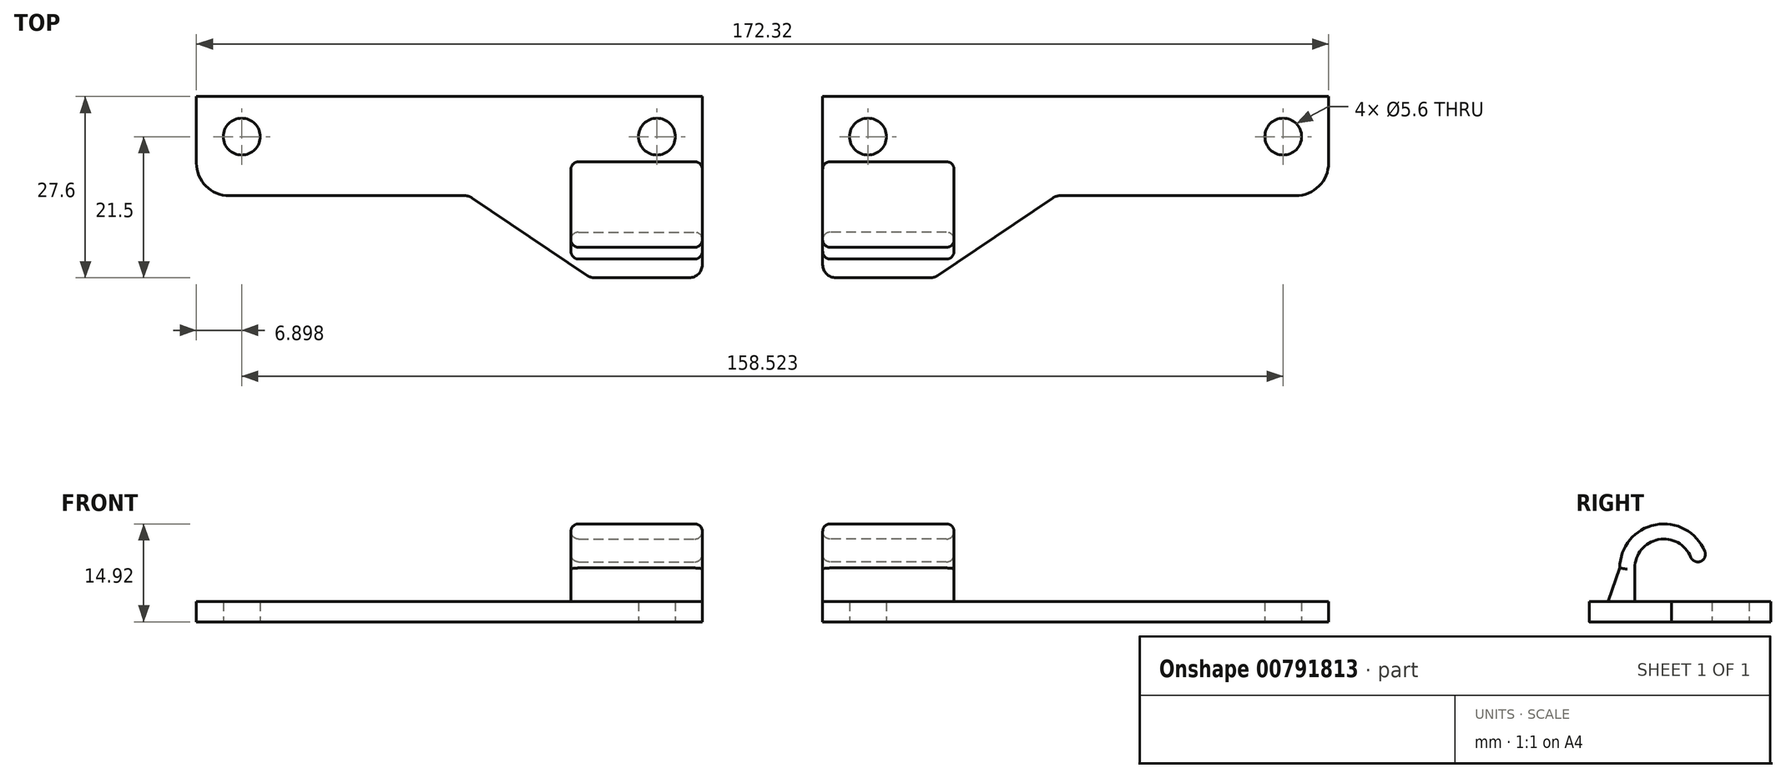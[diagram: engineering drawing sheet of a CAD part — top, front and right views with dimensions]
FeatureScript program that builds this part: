
annotation { "Feature Type Name" : "Feature", "Feature Type Description" : "" }
export const myFeature = defineFeature(function(context is Context, id is Id, definition is map)
    precondition{}
    {
        {
            var Q0;
            Q0=qCreatedBy(makeId("Top.planeOp"),FACE);
            var sketch = newSketch(context, id + "F0", { "sketchPlane" : qUnion([Q0])});
            skLineSegment(sketch, "E0.bottom", {"start": v(-29.06, 27.5) * mm, "end": v(37.94, 27.5) * mm});
            skCircle(sketch, "E1", {"center": v(-27.16, 21.4) * mm, "radius": 2.8 * mm});
            skLineSegment(sketch, "E2", {"start": v(36.74, 27.5) * mm, "end": v(36.74, 21.3) * mm});
            skCircle(sketch, "E3", {"center": v(36.04, 21.4) * mm, "radius": 2.8 * mm});
            skPoint(sketch, "E4.visualSharp", {"position": v(-34.06, 27.5) * mm});
            skPoint(sketch, "E5.visualSharp", {"position": v(42.94, 27.5) * mm});
            skLineSegment(sketch, "E6", {"start": v(-34.06, 22.5) * mm, "end": v(-34.06, 17.4) * mm});
            skLineSegment(sketch, "E7", {"start": v(42.94, 12.4) * mm, "end": v(42.94, 22.5) * mm});
            skLineSegment(sketch, "E8", {"start": v(-34.06, 27.5) * mm, "end": v(-34.06, 22.5) * mm});
            skLineSegment(sketch, "E9", {"start": v(-29.06, 27.5) * mm, "end": v(-34.06, 27.5) * mm});
            skPoint(sketch, "E10.visualSharp", {"position": v(-34.06, 12.4) * mm});
            skArc(sketch, "E10.filletArc", {"start": v(-34.06, 17.4) * mm, "mid": v(-32.6, 13.86) * mm, "end": v(-29.06, 12.4) * mm});
            skLineSegment(sketch, "E11", {"start": v(37.94, 27.5) * mm, "end": v(42.94, 27.5) * mm});
            skLineSegment(sketch, "E12", {"start": v(42.94, 22.5) * mm, "end": v(42.94, 27.5) * mm});
            skLineSegment(sketch, "E13", {"start": v(42.94, 12.4) * mm, "end": v(42.94, 1.9) * mm});
            skLineSegment(sketch, "E14", {"start": v(26.55, -0.1) * mm, "end": v(40.94, -0.1) * mm});
            skLineSegment(sketch, "E15", {"start": v(25.43, 0.24) * mm, "end": v(7.9, 12.06) * mm});
            skLineSegment(sketch, "E16", {"start": v(-29.06, 12.4) * mm, "end": v(6.78, 12.4) * mm});
            skPoint(sketch, "E17.visualSharp", {"position": v(42.94, -0.1) * mm});
            skArc(sketch, "E17.filletArc", {"start": v(40.94, -0.1) * mm, "mid": v(42.35, 0.49) * mm, "end": v(42.94, 1.9) * mm});
            skPoint(sketch, "E18.visualSharp", {"position": v(25.94, -0.1) * mm});
            skArc(sketch, "E18.filletArc", {"start": v(25.43, 0.24) * mm, "mid": v(25.97, -0.01) * mm, "end": v(26.55, -0.1) * mm});
            skPoint(sketch, "E19.visualSharp", {"position": v(7.4, 12.4) * mm});
            skArc(sketch, "E19.filletArc", {"start": v(7.9, 12.06) * mm, "mid": v(7.36, 12.31) * mm, "end": v(6.78, 12.4) * mm});
            skSolve(sketch);
        }
        {
            var Q0;
            Q0=qSketchRegion(id+"F0",true);
            extrude(context, id + "F1", {"entities" : qUnion([Q0]), "depth" : 3.1 * mm, "offsetDistance" : 25 * mm});
        }
        {
            var Q0;
            Q0=makeQuery(id+"F1.opExtrude","CAP_FACE",FACE,{"disambiguationData":[OSD([sQuery(id+"F0.wireOp",EDGE,"E0.bottom"),sQuery(id+"F0.wireOp",EDGE,"E1"),sQuery(id+"F0.wireOp",EDGE,"E3"),sQuery(id+"F0.wireOp",EDGE,"E6"),sQuery(id+"F0.wireOp",EDGE,"E7"),sQuery(id+"F0.wireOp",EDGE,"E8"),sQuery(id+"F0.wireOp",EDGE,"E9"),sQuery(id+"F0.wireOp",EDGE,"E10.filletArc"),sQuery(id+"F0.wireOp",EDGE,"E11"),sQuery(id+"F0.wireOp",EDGE,"E12"),sQuery(id+"F0.wireOp",EDGE,"E13"),sQuery(id+"F0.wireOp",EDGE,"E14"),sQuery(id+"F0.wireOp",EDGE,"E15"),sQuery(id+"F0.wireOp",EDGE,"E16"),sQuery(id+"F0.wireOp",EDGE,"E17.filletArc"),sQuery(id+"F0.wireOp",EDGE,"E18.filletArc"),sQuery(id+"F0.wireOp",EDGE,"E19.filletArc")])],"isStart":false});
            var sketch = newSketch(context, id + "F2", { "sketchPlane" : qUnion([Q0])});
            skLineSegment(sketch, "E20.bottom", {"start": v(22.94, 6.84) * mm, "end": v(42.94, 6.84) * mm});
            skLineSegment(sketch, "E20.top", {"start": v(22.94, 4.54) * mm, "end": v(42.94, 4.54) * mm});
            skLineSegment(sketch, "E20.left", {"start": v(22.94, 6.84) * mm, "end": v(22.94, 4.54) * mm});
            skLineSegment(sketch, "E20.right", {"start": v(42.94, 6.84) * mm, "end": v(42.94, 4.54) * mm});
            skSolve(sketch);
        }
        {
            var Q0;
            Q0=qSketchRegion(id+"F2",true);
            extrude(context, id + "F3", {"entities" : qUnion([Q0]), "operationType" : NewBodyOperationType.ADD, "depth" : 5.1 * mm, "offsetDistance" : 25 * mm});
        }
        {
            var Q0;
            Q0=makeQuery(id+"F3.opExtrude","CAP_FACE",FACE,{"disambiguationData":[OSD([sQuery(id+"F2.wireOp",EDGE,"E20.bottom"),sQuery(id+"F2.wireOp",EDGE,"E20.top"),sQuery(id+"F2.wireOp",EDGE,"E20.left"),sQuery(id+"F2.wireOp",EDGE,"E20.right")])],"isStart":false});
            var sketch = newSketch(context, id + "F4", { "sketchPlane" : qUnion([Q0])});
            skLineSegment(sketch, "E21", {"start": v(22.94, 11.25) * mm, "end": v(42.94, 11.25) * mm});
            skSolve(sketch);
        }
        {
            var Q0;
            Q0=makeQuery(id+"F3.opExtrude","CAP_FACE",FACE,{"disambiguationData":[OSD([sQuery(id+"F2.wireOp",EDGE,"E20.bottom"),sQuery(id+"F2.wireOp",EDGE,"E20.top"),sQuery(id+"F2.wireOp",EDGE,"E20.left"),sQuery(id+"F2.wireOp",EDGE,"E20.right")])],"isStart":false});
            var Q1;
            Q1=sQuery(id+"F4.wireOp",EDGE,"E21");
            revolve(context, id + "F5", {"operationType" : NewBodyOperationType.ADD, "surfaceOperationType" : NewSurfaceOperationType.NEW, "entities" : qUnion([Q0]), "axis" : qUnion([Q1]), "revolveType" : RevolveType.ONE_DIRECTION, "oppositeDirection" : true, "angle" : 170 * degree});
        }
        {
            var Q0;
            Q0=makeQuery(id+"F5.opRevolve","CAP_EDGE",EDGE,{"disambiguationData":[OSD([sQuery(id+"F2.wireOp",EDGE,"E20.bottom")])],"isStart":false});
            var Q1;
            Q1=makeQuery(id+"F5.opRevolve","CAP_EDGE",EDGE,{"disambiguationData":[OSD([sQuery(id+"F2.wireOp",EDGE,"E20.top")])],"isStart":false});
            fillet(context, id + "F6", {"entities" : qUnion([Q0, Q1]), "radius" : 1.15 * mm, "tangentPropagation" : true, "allowEdgeOverflow" : false});
        }
        {
            var Q0;
            {var subQ0=sQuery(id+"F2.wireOp",EDGE,"E20.left");Q0=makeQuery(id+"F5.boolean.opBoolean","MERGE",FACE,{"derivedFrom":[makeQuery(id+"F3.opExtrude","SWEPT_FACE",FACE,{"disambiguationData":[OSD([subQ0])]}),makeQuery(id+"F5.opRevolve","SWEPT_FACE",FACE,{"disambiguationData":[OSD([subQ0])]})]});}
            var sketch = newSketch(context, id + "F7", { "sketchPlane" : qUnion([Q0])});
            skLineSegment(sketch, "E22", {"start": v(-4.54, 8.2) * mm, "end": v(-2.74, 3.1) * mm});
            skLineSegment(sketch, "E23", {"start": v(-2.74, 3.1) * mm, "end": v(-4.54, 3.1) * mm});
            skLineSegment(sketch, "E24", {"start": v(-4.54, 8.2) * mm, "end": v(-4.54, 3.1) * mm});
            skSolve(sketch);
        }
        {
            var Q0;
            Q0=qSketchRegion(id+"F7",true);
            extrude(context, id + "F8", {"entities" : qUnion([Q0]), "operationType" : NewBodyOperationType.ADD, "oppositeDirection" : true, "depth" : 20 * mm, "offsetDistance" : 25 * mm});
        }
        {
            var Q0;
            Q0=makeQuery(id+"F8.opExtrude","CAP_EDGE",EDGE,{"disambiguationData":[OSD([sQuery(id+"F7.wireOp",EDGE,"E22")])],"isStart":true});
            var Q1;
            Q1=makeQuery(id+"F5.opRevolve","SWEPT_EDGE",EDGE,{"disambiguationData":[OSD([sQuery(id+"F2.wireOp",EDGE,"E20.top"),sQuery(id+"F2.wireOp",EDGE,"E20.left")])]});
            var Q2;
            Q2=makeQuery(id+"F8.opExtrude","CAP_EDGE",EDGE,{"disambiguationData":[OSD([sQuery(id+"F7.wireOp",EDGE,"E22")])],"isStart":false});
            var Q3;
            Q3=makeQuery(id+"F5.opRevolve","SWEPT_EDGE",EDGE,{"disambiguationData":[OSD([sQuery(id+"F2.wireOp",EDGE,"E20.top"),sQuery(id+"F2.wireOp",EDGE,"E20.right")])]});
            fillet(context, id + "F9", {"entities" : qUnion([Q0, Q1, Q2, Q3]), "radius" : 1.14 * mm, "tangentPropagation" : true, "allowEdgeOverflow" : false});
        }
        {
            var Q0;
            Q0=makeQuery(id+"F1.opExtrude","SWEPT_BODY",BODY,{"disambiguationData":[OSD([sQuery(id+"F0.wireOp",EDGE,"E0.bottom"),sQuery(id+"F0.wireOp",EDGE,"E1"),sQuery(id+"F0.wireOp",EDGE,"E3"),sQuery(id+"F0.wireOp",EDGE,"E6"),sQuery(id+"F0.wireOp",EDGE,"E7"),sQuery(id+"F0.wireOp",EDGE,"E8"),sQuery(id+"F0.wireOp",EDGE,"E9"),sQuery(id+"F0.wireOp",EDGE,"E10.filletArc"),sQuery(id+"F0.wireOp",EDGE,"E11"),sQuery(id+"F0.wireOp",EDGE,"E12"),sQuery(id+"F0.wireOp",EDGE,"E13"),sQuery(id+"F0.wireOp",EDGE,"E14"),sQuery(id+"F0.wireOp",EDGE,"E15"),sQuery(id+"F0.wireOp",EDGE,"E16"),sQuery(id+"F0.wireOp",EDGE,"E17.filletArc"),sQuery(id+"F0.wireOp",EDGE,"E18.filletArc"),sQuery(id+"F0.wireOp",EDGE,"E19.filletArc")])]});
            transform(context, id + "F10", {"entities" : qUnion([Q0]), "transformType" : TransformType.TRANSLATION_3D, "dx" : -52.1 * mm, "dy" : 0 * mm, "dz" : 0 * mm, "makeCopy" : false});
        }
        {
            var Q0;
            Q0=makeQuery(id+"F1.opExtrude","SWEPT_BODY",BODY,{"disambiguationData":[OSD([sQuery(id+"F0.wireOp",EDGE,"E0.bottom"),sQuery(id+"F0.wireOp",EDGE,"E1"),sQuery(id+"F0.wireOp",EDGE,"E3"),sQuery(id+"F0.wireOp",EDGE,"E6"),sQuery(id+"F0.wireOp",EDGE,"E7"),sQuery(id+"F0.wireOp",EDGE,"E8"),sQuery(id+"F0.wireOp",EDGE,"E9"),sQuery(id+"F0.wireOp",EDGE,"E10.filletArc"),sQuery(id+"F0.wireOp",EDGE,"E11"),sQuery(id+"F0.wireOp",EDGE,"E12"),sQuery(id+"F0.wireOp",EDGE,"E13"),sQuery(id+"F0.wireOp",EDGE,"E14"),sQuery(id+"F0.wireOp",EDGE,"E15"),sQuery(id+"F0.wireOp",EDGE,"E16"),sQuery(id+"F0.wireOp",EDGE,"E17.filletArc"),sQuery(id+"F0.wireOp",EDGE,"E18.filletArc"),sQuery(id+"F0.wireOp",EDGE,"E19.filletArc")])]});
            var Q1;
            Q1=qCreatedBy(makeId("Right.planeOp"),FACE);
            mirror(context, id + "F11", {"entities" : qUnion([Q0]), "mirrorPlane" : qUnion([Q1])});
        }
    });
